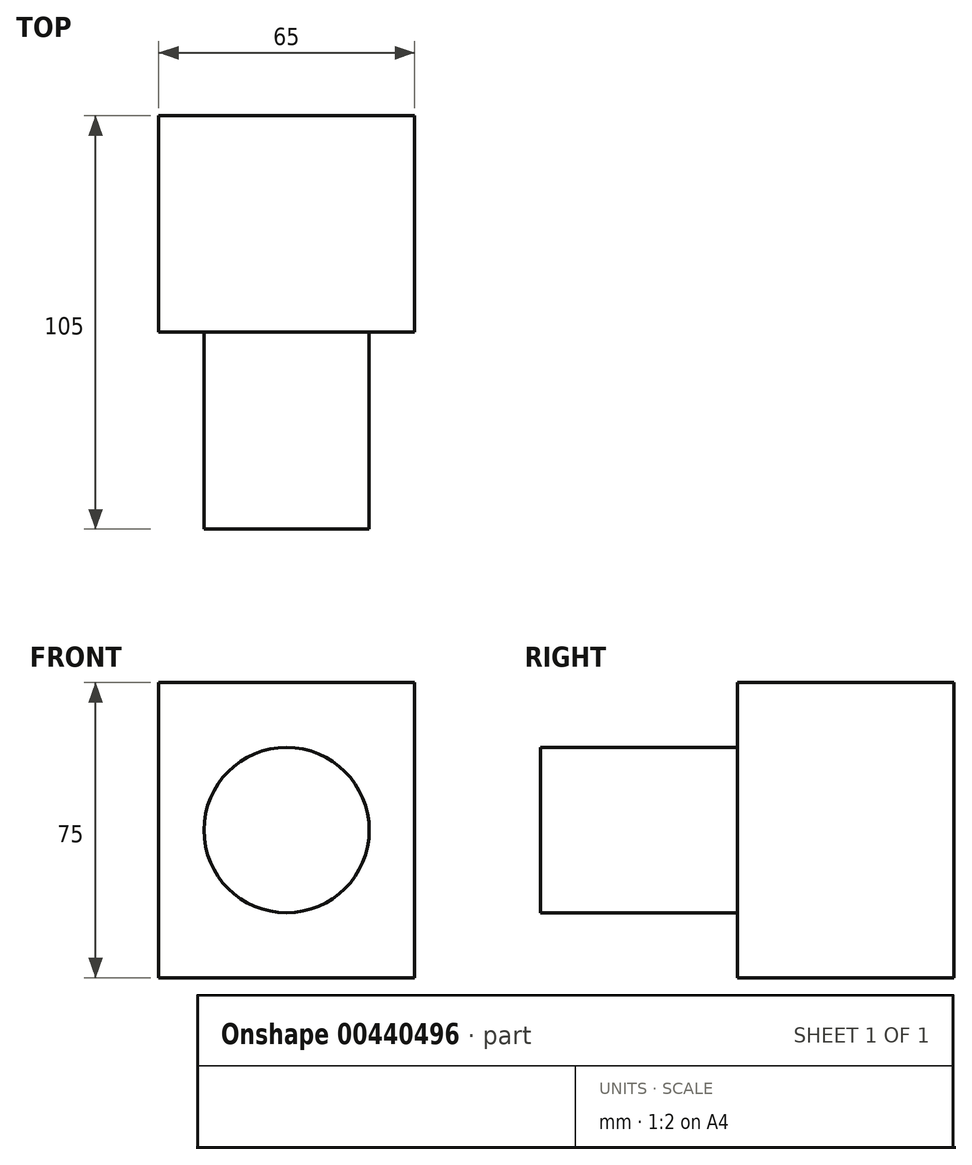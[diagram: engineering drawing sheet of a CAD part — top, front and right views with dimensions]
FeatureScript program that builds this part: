
annotation { "Feature Type Name" : "Feature", "Feature Type Description" : "" }
export const myFeature = defineFeature(function(context is Context, id is Id, definition is map)
    precondition{}
    {
        {
            var Q0;
            Q0=qCreatedBy(makeId("Front.planeOp"),FACE);
            var sketch = newSketch(context, id + "F0", { "sketchPlane" : qUnion([Q0])});
            skLineSegment(sketch, "E0.bottom", {"start": v(32.5, 37.5) * mm, "end": v(-32.5, 37.5) * mm});
            skLineSegment(sketch, "E0.top", {"start": v(32.5, -37.5) * mm, "end": v(-32.5, -37.5) * mm});
            skLineSegment(sketch, "E0.left", {"start": v(32.5, 37.5) * mm, "end": v(32.5, -37.5) * mm});
            skLineSegment(sketch, "E0.right", {"start": v(-32.5, 37.5) * mm, "end": v(-32.5, -37.5) * mm});
            skPoint(sketch, "E0.middle", {"position": v(0, 0) * mm});
            skSolve(sketch);
        }
        {
            var Q0;
            Q0 = qSketchRegion(id + "F0", true);
            extrude(context, id + "F1", {"entities" : qUnion([Q0]), "offsetDistance" : 25 * mm, "depth" : 55 * mm});
        }
        {
            var Q0;
            Q0=makeQuery(id+"F1.opExtrude","CAP_FACE",FACE,{"disambiguationData":[OSD([sQuery(id+"F0.wireOp",EDGE,"E0.bottom"),sQuery(id+"F0.wireOp",EDGE,"E0.top"),sQuery(id+"F0.wireOp",EDGE,"E0.left"),sQuery(id+"F0.wireOp",EDGE,"E0.right")])],"isStart":false});
            var sketch = newSketch(context, id + "F2", { "sketchPlane" : qUnion([Q0])});
            skCircle(sketch, "E1", {"center": v(0, 0) * mm, "radius": 21 * mm});
            skSolve(sketch);
        }
        {
            var Q0;
            Q0 = qSketchRegion(id + "F2", true);
            extrude(context, id + "F3", {"entities" : qUnion([Q0]), "operationType" : NewBodyOperationType.ADD, "offsetDistance" : 25 * mm, "depth" : 50 * mm});
        }
    });
